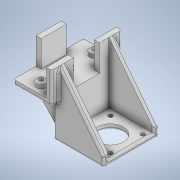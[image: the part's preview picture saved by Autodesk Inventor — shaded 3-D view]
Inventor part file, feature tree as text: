
AUTODESK INVENTOR PART (.ipt)
format: ipt  version: 2020 (Build 240168000, 168)  size: 538,624 bytes
history: native  units: in
note: dims shown in document units (in); Inventor stores cm internally (conversion verified against a paired STEP export)
features: extrude x11, sketch x11, fillet x5, chamfer x1
ambient origin geometry x8: Origin, YZ Plane, XZ Plane, XY Plane, X Axis, Y Axis, Z Axis, Center Point
bodies: Solid1 (feature_tree)
feature tree (28):
  extrude  "Extrusion1"  Depth=2.6378in
  extrude  "Extrusion2"  Depth=0.1969in
  extrude  "Extrusion6"  Depth=0.1969in
  extrude  "Extrusion8"  Depth=1.0in TaperAngle=0.0deg
  chamfer  "Chamfer1"  Distance=1.0in
  extrude  "Extrusion9"  Depth=0.3406in
  extrude  "Extrusion10"  Depth=0.1969in TaperAngle=0.0deg
  extrude  "Extrusion11"  Depth=0.0787in
  extrude  "Extrusion12"  Depth=0.1575in
  extrude  "Extrusion13"  Depth=0.0787in
  extrude  "Extrusion14"  Depth=0.0787in
  fillet  "Fillet4"  Radius=0.2362in
  fillet  "Fillet5"  Radius=0.0984in
  fillet  "Fillet6"  Radius=0.1969in
  fillet  "Fillet7"  Radius=2.0866in
  extrude  "Extrusion15"  Depth=0.0787in
  fillet  "Fillet8"  Radius=0.1969in
  sketch  "Sketch1"  dims[d0=1.4331in d1=2.6378in]
  sketch  "Sketch2"  dims[d2=0.1969in d3=0.0in d4=0.1969in]
  sketch  "Sketch6"  dims[d5=0.8268in d6=0.1969in]
  sketch  "Sketch8"  dims[d7=0.8268in d8=1.0in d9=0.0in]
  sketch  "Sketch9"  dims[d26=0.1969in]
  sketch  "Sketch10"  dims[d27=0.9449in d28=1.0in d29=0.0in]
  sketch  "Sketch11"  dims[d37=0.3406in d38=0.3406in]
  sketch  "Sketch12"  dims[d39=0.3406in d40=0.1969in d41=0.0in]
  sketch  "Sketch13"  dims[d42=0.0591in d43=0.0787in d44=45.0deg d45=0.1575in]
  sketch  "Sketch14"  dims[d46=0.1575in d47=0.1575in]
  sketch  "Sketch15"  dims[d48=0.7874in d49=0.0in d50=0.2362in d51=0.2362in d52=0.2362in d53=0.0984in d54=0.0in d55=0.1969in d56=2.0866in d57=0.1969in d58=0.1969in d59=1.2992in d60=0.0in d61=0.1969in d62=0.1969in d63=0.1969in d64=1.811in d65=0.0in d66=3.937in d67=0.0in d68=0.1575in d69=0.1575in d70=0.1575in d71=0.1575in d72=0.9843in d73=3.937in d74=0.0in d75=0.0787in d76=0.0787in d77=0.0787in d78=0.0787in d79=0.1181in d80=3.937in d81=0.0in d82=0.0787in d10=0.0197in d11=0.0344in d13=0.0197in d14=0.0344in d15=0.0197in d16=0.0344in d83=0.0344in]
